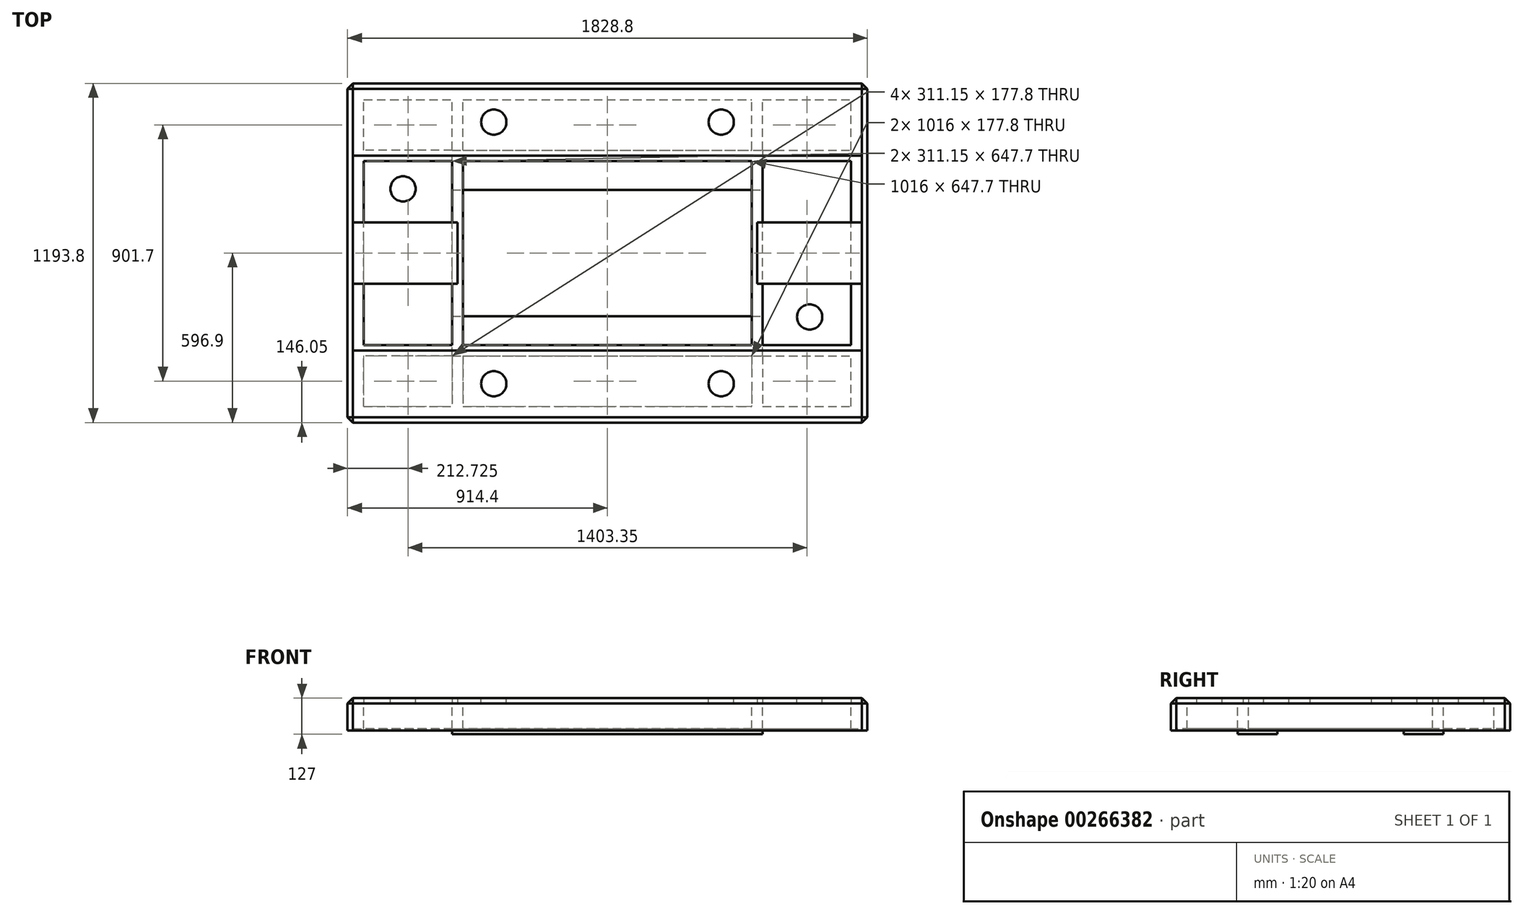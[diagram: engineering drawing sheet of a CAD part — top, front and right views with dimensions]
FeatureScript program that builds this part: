
annotation { "Feature Type Name" : "Feature", "Feature Type Description" : "" }
export const myFeature = defineFeature(function(context is Context, id is Id, definition is map)
    precondition{}
    {
        {
            var Q0;
            Q0=qCreatedBy(makeId("Top.planeOp"),FACE);
            var sketch = newSketch(context, id + "F0", { "sketchPlane" : qUnion([Q0])});
            skLineSegment(sketch, "E0.bottom", {"start": v(508, 323.85) * mm, "end": v(-508, 323.85) * mm});
            skLineSegment(sketch, "E0.top", {"start": v(508, -323.85) * mm, "end": v(-508, -323.85) * mm});
            skLineSegment(sketch, "E0.left", {"start": v(508, 323.85) * mm, "end": v(508, -323.85) * mm});
            skLineSegment(sketch, "E0.right", {"start": v(-508, 323.85) * mm, "end": v(-508, -323.85) * mm});
            skPoint(sketch, "E0.middle", {"position": v(0, 0) * mm});
            skLineSegment(sketch, "E1.bottom", {"start": v(-546.1, -361.95) * mm, "end": v(546.1, -361.95) * mm});
            skLineSegment(sketch, "E1.top", {"start": v(-546.1, 361.95) * mm, "end": v(546.1, 361.95) * mm});
            skLineSegment(sketch, "E1.left", {"start": v(-546.1, -361.95) * mm, "end": v(-546.1, 361.95) * mm});
            skLineSegment(sketch, "E1.right", {"start": v(546.1, -361.95) * mm, "end": v(546.1, 361.95) * mm});
            skLineSegment(sketch, "E2.bottom", {"start": v(-895.35, 577.85) * mm, "end": v(895.35, 577.85) * mm});
            skLineSegment(sketch, "E2.top", {"start": v(-895.35, -577.85) * mm, "end": v(895.35, -577.85) * mm});
            skLineSegment(sketch, "E2.left", {"start": v(-895.35, 577.85) * mm, "end": v(-895.35, -577.85) * mm});
            skLineSegment(sketch, "E2.right", {"start": v(895.35, 577.85) * mm, "end": v(895.35, -577.85) * mm});
            skLineSegment(sketch, "E3.bottom", {"start": v(-857.25, -539.75) * mm, "end": v(857.25, -539.75) * mm});
            skLineSegment(sketch, "E3.top", {"start": v(-857.25, 539.75) * mm, "end": v(857.25, 539.75) * mm});
            skLineSegment(sketch, "E3.left", {"start": v(-857.25, -539.75) * mm, "end": v(-857.25, 539.75) * mm});
            skLineSegment(sketch, "E3.right", {"start": v(857.25, -539.75) * mm, "end": v(857.25, 539.75) * mm});
            skLineSegment(sketch, "E4", {"start": v(-546.1, 361.95) * mm, "end": v(-895.35, 361.95) * mm});
            skLineSegment(sketch, "E5", {"start": v(-508, 323.85) * mm, "end": v(-895.35, 323.85) * mm});
            skLineSegment(sketch, "E6", {"start": v(-546.1, 361.95) * mm, "end": v(-546.1, 577.85) * mm});
            skLineSegment(sketch, "E7", {"start": v(-508, 323.85) * mm, "end": v(-508, 577.85) * mm});
            skLineSegment(sketch, "E8", {"start": v(546.1, 361.95) * mm, "end": v(546.1, 577.85) * mm});
            skLineSegment(sketch, "E9", {"start": v(508, 323.85) * mm, "end": v(508, 577.85) * mm});
            skLineSegment(sketch, "E10", {"start": v(508, -323.85) * mm, "end": v(508, -577.85) * mm});
            skLineSegment(sketch, "E11", {"start": v(546.1, -361.95) * mm, "end": v(546.1, -577.85) * mm});
            skLineSegment(sketch, "E12", {"start": v(546.1, -361.95) * mm, "end": v(895.35, -361.95) * mm});
            skLineSegment(sketch, "E13", {"start": v(508, -323.85) * mm, "end": v(895.35, -323.85) * mm});
            skLineSegment(sketch, "E14", {"start": v(-546.1, -361.95) * mm, "end": v(-895.35, -361.95) * mm});
            skLineSegment(sketch, "E15", {"start": v(-508, -323.85) * mm, "end": v(-895.35, -323.85) * mm});
            skLineSegment(sketch, "E16", {"start": v(546.1, 361.95) * mm, "end": v(895.35, 361.95) * mm});
            skLineSegment(sketch, "E17", {"start": v(508, 323.85) * mm, "end": v(895.35, 323.85) * mm});
            skLineSegment(sketch, "E18", {"start": v(-546.1, -361.95) * mm, "end": v(-546.1, -577.85) * mm});
            skLineSegment(sketch, "E19", {"start": v(-508, -323.85) * mm, "end": v(-508, -577.85) * mm});
            skSolve(sketch);
        }
        {
            var Q0;
            Q0 = qSketchRegion(id + "F0", true);
            var Q1;
            {var subQ3=sQuery(id+"F0.wireOp",EDGE,"E5");var subQ5=sQuery(id+"F0.wireOp",EDGE,"E3.left");var subQ6=makeQuery(id+"F0.imprint","INTERSECT",VERTEX,{"derivedFrom":[subQ5,subQ3]});Q1=makeQuery(id+"F0.imprint","IMPRINT",FACE,{"disambiguationData":[TD([[makeQuery(id+"F0.imprint","IMPRINT",EDGE,{"disambiguationData":[TD([[subQ6,-1.0]])],"derivedFrom":subQ5}),-1.0]])]});}
            var Q2;
            {var subQ0=sQuery(id+"F0.wireOp",EDGE,"E6");var subQ5=sQuery(id+"F0.wireOp",EDGE,"E3.top");var subQ7=makeQuery(id+"F0.imprint","INTERSECT",VERTEX,{"derivedFrom":[subQ5,subQ0]});Q2=makeQuery(id+"F0.imprint","IMPRINT",FACE,{"disambiguationData":[TD([[makeQuery(id+"F0.imprint","IMPRINT",EDGE,{"disambiguationData":[TD([[subQ7,-1.0]])],"derivedFrom":subQ5}),-1.0]])]});}
            var Q3;
            {var subQ1=sQuery(id+"F0.wireOp",EDGE,"E1.top");var subQ3=sQuery(id+"F0.wireOp",EDGE,"E7");var subQ4=makeQuery(id+"F0.imprint","INTERSECT",VERTEX,{"derivedFrom":[subQ1,subQ3]});Q3=makeQuery(id+"F0.imprint","IMPRINT",FACE,{"disambiguationData":[TD([[makeQuery(id+"F0.imprint","IMPRINT",EDGE,{"disambiguationData":[TD([[subQ4,1.0]])],"derivedFrom":subQ1}),-1.0]])]});}
            var Q4;
            {var subQ0=sQuery(id+"F0.wireOp",EDGE,"E0.right");Q4=makeQuery(id+"F0.imprint","IMPRINT",FACE,{"disambiguationData":[TD([[makeQuery(id+"F0.imprint","IMPRINT",EDGE,{"derivedFrom":subQ0}),-1.0]])]});}
            var Q5;
            {var subQ0=sQuery(id+"F0.wireOp",EDGE,"E14");var subQ5=sQuery(id+"F0.wireOp",EDGE,"E3.left");var subQ6=makeQuery(id+"F0.imprint","INTERSECT",VERTEX,{"derivedFrom":[subQ5,subQ0]});Q5=makeQuery(id+"F0.imprint","IMPRINT",FACE,{"disambiguationData":[TD([[makeQuery(id+"F0.imprint","IMPRINT",EDGE,{"disambiguationData":[TD([[subQ6,-1.0]])],"derivedFrom":subQ5}),-1.0]])]});}
            var Q6;
            {var subQ0=sQuery(id+"F0.wireOp",EDGE,"E18");var subQ5=sQuery(id+"F0.wireOp",EDGE,"E3.bottom");var subQ6=makeQuery(id+"F0.imprint","INTERSECT",VERTEX,{"derivedFrom":[subQ5,subQ0]});Q6=makeQuery(id+"F0.imprint","IMPRINT",FACE,{"disambiguationData":[TD([[makeQuery(id+"F0.imprint","IMPRINT",EDGE,{"disambiguationData":[TD([[subQ6,-1.0]])],"derivedFrom":subQ5}),1.0]])]});}
            var Q7;
            {var subQ1=sQuery(id+"F0.wireOp",EDGE,"E1.bottom");var subQ3=sQuery(id+"F0.wireOp",EDGE,"E19");var subQ4=makeQuery(id+"F0.imprint","INTERSECT",VERTEX,{"derivedFrom":[subQ1,subQ3]});Q7=makeQuery(id+"F0.imprint","IMPRINT",FACE,{"disambiguationData":[TD([[makeQuery(id+"F0.imprint","IMPRINT",EDGE,{"disambiguationData":[TD([[subQ4,1.0]])],"derivedFrom":subQ1}),1.0]])]});}
            var Q8;
            {var subQ0=sQuery(id+"F0.wireOp",EDGE,"E0.top");Q8=makeQuery(id+"F0.imprint","IMPRINT",FACE,{"disambiguationData":[TD([[makeQuery(id+"F0.imprint","IMPRINT",EDGE,{"derivedFrom":subQ0}),1.0]])]});}
            var Q9;
            {var subQ3=sQuery(id+"F0.wireOp",EDGE,"E10");var subQ5=sQuery(id+"F0.wireOp",EDGE,"E3.bottom");var subQ6=makeQuery(id+"F0.imprint","INTERSECT",VERTEX,{"derivedFrom":[subQ5,subQ3]});Q9=makeQuery(id+"F0.imprint","IMPRINT",FACE,{"disambiguationData":[TD([[makeQuery(id+"F0.imprint","IMPRINT",EDGE,{"disambiguationData":[TD([[subQ6,-1.0]])],"derivedFrom":subQ5}),1.0]])]});}
            var Q10;
            {var subQ1=sQuery(id+"F0.wireOp",EDGE,"E1.bottom");var subQ3=sQuery(id+"F0.wireOp",EDGE,"E10");var subQ4=makeQuery(id+"F0.imprint","INTERSECT",VERTEX,{"derivedFrom":[subQ1,subQ3]});Q10=makeQuery(id+"F0.imprint","IMPRINT",FACE,{"disambiguationData":[TD([[makeQuery(id+"F0.imprint","IMPRINT",EDGE,{"disambiguationData":[TD([[subQ4,-1.0]])],"derivedFrom":subQ1}),1.0]])]});}
            var Q11;
            {var subQ0=sQuery(id+"F0.wireOp",EDGE,"E12");var subQ5=sQuery(id+"F0.wireOp",EDGE,"E3.right");var subQ6=makeQuery(id+"F0.imprint","INTERSECT",VERTEX,{"derivedFrom":[subQ5,subQ0]});Q11=makeQuery(id+"F0.imprint","IMPRINT",FACE,{"disambiguationData":[TD([[makeQuery(id+"F0.imprint","IMPRINT",EDGE,{"disambiguationData":[TD([[subQ6,-1.0]])],"derivedFrom":subQ5}),1.0]])]});}
            var Q12;
            {var subQ0=sQuery(id+"F0.wireOp",EDGE,"E0.left");Q12=makeQuery(id+"F0.imprint","IMPRINT",FACE,{"disambiguationData":[TD([[makeQuery(id+"F0.imprint","IMPRINT",EDGE,{"derivedFrom":subQ0}),1.0]])]});}
            var Q13;
            {var subQ1=sQuery(id+"F0.wireOp",EDGE,"E1.top");var subQ3=sQuery(id+"F0.wireOp",EDGE,"E9");var subQ4=makeQuery(id+"F0.imprint","INTERSECT",VERTEX,{"derivedFrom":[subQ1,subQ3]});Q13=makeQuery(id+"F0.imprint","IMPRINT",FACE,{"disambiguationData":[TD([[makeQuery(id+"F0.imprint","IMPRINT",EDGE,{"disambiguationData":[TD([[subQ4,-1.0]])],"derivedFrom":subQ1}),-1.0]])]});}
            var Q14;
            {var subQ3=sQuery(id+"F0.wireOp",EDGE,"E9");var subQ5=sQuery(id+"F0.wireOp",EDGE,"E3.top");var subQ6=makeQuery(id+"F0.imprint","INTERSECT",VERTEX,{"derivedFrom":[subQ5,subQ3]});Q14=makeQuery(id+"F0.imprint","IMPRINT",FACE,{"disambiguationData":[TD([[makeQuery(id+"F0.imprint","IMPRINT",EDGE,{"disambiguationData":[TD([[subQ6,-1.0]])],"derivedFrom":subQ5}),-1.0]])]});}
            var Q15;
            {var subQ3=sQuery(id+"F0.wireOp",EDGE,"E17");var subQ5=sQuery(id+"F0.wireOp",EDGE,"E3.right");var subQ6=makeQuery(id+"F0.imprint","INTERSECT",VERTEX,{"derivedFrom":[subQ5,subQ3]});Q15=makeQuery(id+"F0.imprint","IMPRINT",FACE,{"disambiguationData":[TD([[makeQuery(id+"F0.imprint","IMPRINT",EDGE,{"disambiguationData":[TD([[subQ6,-1.0]])],"derivedFrom":subQ5}),1.0]])]});}
            var Q16;
            {var subQ0=sQuery(id+"F0.wireOp",EDGE,"E0.bottom");Q16=makeQuery(id+"F0.imprint","IMPRINT",FACE,{"disambiguationData":[TD([[makeQuery(id+"F0.imprint","IMPRINT",EDGE,{"derivedFrom":subQ0}),-1.0]])]});}
            extrude(context, id + "F1", {"entities" : qUnion([Q0, Q1, Q2, Q3, Q4, Q5, Q6, Q7, Q8, Q9, Q10, Q11, Q12, Q13, Q14, Q15, Q16]), "oppositeDirection" : true, "depth" : 88.9 * mm});
        }
        {
            var Q0;
            Q0=makeQuery(id+"F1.opExtrude","CAP_FACE",FACE,{"disambiguationData":[OSD([sQuery(id+"F0.wireOp",EDGE,"E0.bottom"),sQuery(id+"F0.wireOp",EDGE,"E0.top"),sQuery(id+"F0.wireOp",EDGE,"E0.left"),sQuery(id+"F0.wireOp",EDGE,"E0.right"),sQuery(id+"F0.wireOp",EDGE,"E1.bottom"),sQuery(id+"F0.wireOp",EDGE,"E1.top"),sQuery(id+"F0.wireOp",EDGE,"E1.left"),sQuery(id+"F0.wireOp",EDGE,"E1.right"),sQuery(id+"F0.wireOp",EDGE,"E2.bottom"),sQuery(id+"F0.wireOp",EDGE,"E2.top"),sQuery(id+"F0.wireOp",EDGE,"E2.left"),sQuery(id+"F0.wireOp",EDGE,"E2.right"),sQuery(id+"F0.wireOp",EDGE,"E3.bottom"),sQuery(id+"F0.wireOp",EDGE,"E3.top"),sQuery(id+"F0.wireOp",EDGE,"E3.left"),sQuery(id+"F0.wireOp",EDGE,"E3.right"),sQuery(id+"F0.wireOp",EDGE,"E4"),sQuery(id+"F0.wireOp",EDGE,"E5"),sQuery(id+"F0.wireOp",EDGE,"E6"),sQuery(id+"F0.wireOp",EDGE,"E7"),sQuery(id+"F0.wireOp",EDGE,"E8"),sQuery(id+"F0.wireOp",EDGE,"E9"),sQuery(id+"F0.wireOp",EDGE,"E10"),sQuery(id+"F0.wireOp",EDGE,"E11"),sQuery(id+"F0.wireOp",EDGE,"E12"),sQuery(id+"F0.wireOp",EDGE,"E13"),sQuery(id+"F0.wireOp",EDGE,"E14"),sQuery(id+"F0.wireOp",EDGE,"E15"),sQuery(id+"F0.wireOp",EDGE,"E16"),sQuery(id+"F0.wireOp",EDGE,"E17"),sQuery(id+"F0.wireOp",EDGE,"E18"),sQuery(id+"F0.wireOp",EDGE,"E19")])],"isStart":true});
            var sketch = newSketch(context, id + "F2", { "sketchPlane" : qUnion([Q0])});
            skLineSegment(sketch, "E20.bottom", {"start": v(-895.35, 577.85) * mm, "end": v(895.35, 577.85) * mm});
            skLineSegment(sketch, "E20.top", {"start": v(-895.35, 342.9) * mm, "end": v(895.35, 342.9) * mm});
            skLineSegment(sketch, "E20.left", {"start": v(-895.35, 577.85) * mm, "end": v(-895.35, 342.9) * mm});
            skLineSegment(sketch, "E20.right", {"start": v(895.35, 577.85) * mm, "end": v(895.35, 342.9) * mm});
            skLineSegment(sketch, "E21.bottom", {"start": v(-895.35, -577.85) * mm, "end": v(895.35, -577.85) * mm});
            skLineSegment(sketch, "E21.top", {"start": v(-895.35, -342.9) * mm, "end": v(895.35, -342.9) * mm});
            skLineSegment(sketch, "E21.left", {"start": v(-895.35, -577.85) * mm, "end": v(-895.35, -342.9) * mm});
            skLineSegment(sketch, "E21.right", {"start": v(895.35, -577.85) * mm, "end": v(895.35, -342.9) * mm});
            skLineSegment(sketch, "E22.bottom", {"start": v(-895.35, -342.9) * mm, "end": v(-527.05, -342.9) * mm});
            skLineSegment(sketch, "E22.top", {"start": v(-895.35, -107.95) * mm, "end": v(-527.05, -107.95) * mm});
            skLineSegment(sketch, "E22.left", {"start": v(-895.35, -342.9) * mm, "end": v(-895.35, -107.95) * mm});
            skLineSegment(sketch, "E22.right", {"start": v(-527.05, -342.9) * mm, "end": v(-527.05, -107.95) * mm});
            skLineSegment(sketch, "E23.bottom", {"start": v(-895.35, 342.9) * mm, "end": v(-527.05, 342.9) * mm});
            skLineSegment(sketch, "E23.top", {"start": v(-895.35, 107.95) * mm, "end": v(-527.05, 107.95) * mm});
            skLineSegment(sketch, "E23.left", {"start": v(-895.35, 342.9) * mm, "end": v(-895.35, 107.95) * mm});
            skLineSegment(sketch, "E23.right", {"start": v(-527.05, 342.9) * mm, "end": v(-527.05, 107.95) * mm});
            skLineSegment(sketch, "E24.left", {"start": v(-895.35, 107.95) * mm, "end": v(-895.35, -107.95) * mm});
            skLineSegment(sketch, "E24.right", {"start": v(-527.05, 107.95) * mm, "end": v(-527.05, -107.95) * mm});
            skLineSegment(sketch, "E25.bottom", {"start": v(895.35, 342.9) * mm, "end": v(527.05, 342.9) * mm});
            skLineSegment(sketch, "E25.top", {"start": v(895.35, 107.95) * mm, "end": v(527.05, 107.95) * mm});
            skLineSegment(sketch, "E25.left", {"start": v(895.35, 342.9) * mm, "end": v(895.35, 107.95) * mm});
            skLineSegment(sketch, "E25.right", {"start": v(527.05, 342.9) * mm, "end": v(527.05, 107.95) * mm});
            skLineSegment(sketch, "E26.bottom", {"start": v(895.35, -342.9) * mm, "end": v(527.05, -342.9) * mm});
            skLineSegment(sketch, "E26.top", {"start": v(895.35, -107.95) * mm, "end": v(527.05, -107.95) * mm});
            skLineSegment(sketch, "E26.left", {"start": v(895.35, -342.9) * mm, "end": v(895.35, -107.95) * mm});
            skLineSegment(sketch, "E26.right", {"start": v(527.05, -342.9) * mm, "end": v(527.05, -107.95) * mm});
            skLineSegment(sketch, "E27.left", {"start": v(895.35, 107.95) * mm, "end": v(895.35, -107.95) * mm});
            skLineSegment(sketch, "E27.right", {"start": v(527.05, 107.95) * mm, "end": v(527.05, -107.95) * mm});
            skSolve(sketch);
        }
        {
            var Q0;
            Q0=makeQuery(id+"F2.imprint","IMPRINT",FACE,{"disambiguationData":[TD([[makeQuery(id+"F2.imprint","IMPRINT",EDGE,{"derivedFrom":sQuery(id+"F2.wireOp",EDGE,"E20.bottom")}),-1.0]])]});
            var Q1;
            {var subQ4=sQuery(id+"F0.wireOp",EDGE,"E4");Q1=makeQuery(id+"F2.imprint","IMPRINT",FACE,{"disambiguationData":[TD([[makeQuery(id+"F2.imprint","IMPRINT",EDGE,{"derivedFrom":makeQuery(id+"F1.opExtrude","CAP_EDGE",EDGE,{"disambiguationData":[OSD([subQ4])],"isStart":true})}),-1.0]])]});}
            var Q2;
            Q2=makeQuery(id+"F2.imprint","IMPRINT",FACE,{"disambiguationData":[TD([[makeQuery(id+"F2.imprint","IMPRINT",EDGE,{"derivedFrom":makeQuery(id+"F1.opExtrude","CAP_EDGE",EDGE,{"disambiguationData":[OSD([sQuery(id+"F0.wireOp",EDGE,"E1.top")])],"isStart":true})}),1.0]])]});
            var Q3;
            {var subQ0=sQuery(id+"F2.wireOp",EDGE,"E25.top");var subQ4=makeQuery(id+"F1.opExtrude","CAP_EDGE",EDGE,{"disambiguationData":[OSD([sQuery(id+"F0.wireOp",EDGE,"E1.right")])],"isStart":true});var subQ5=makeQuery(id+"F2.imprint","INTERSECT",VERTEX,{"derivedFrom":[subQ4,subQ0]});Q3=makeQuery(id+"F2.imprint","IMPRINT",FACE,{"disambiguationData":[TD([[makeQuery(id+"F2.imprint","IMPRINT",EDGE,{"disambiguationData":[TD([[subQ5,1.0]])],"derivedFrom":subQ4}),-1.0]])]});}
            var Q4;
            {var subQ0=sQuery(id+"F2.wireOp",EDGE,"E27.left");Q4=makeQuery(id+"F2.imprint","IMPRINT",FACE,{"disambiguationData":[TD([[makeQuery(id+"F2.imprint","IMPRINT",EDGE,{"derivedFrom":subQ0}),-1.0]])]});}
            var Q5;
            {var subQ0=sQuery(id+"F2.wireOp",EDGE,"E27.right");Q5=makeQuery(id+"F2.imprint","IMPRINT",FACE,{"disambiguationData":[TD([[makeQuery(id+"F2.imprint","IMPRINT",EDGE,{"derivedFrom":subQ0}),1.0]])]});}
            var Q6;
            {var subQ0=sQuery(id+"F2.wireOp",EDGE,"E23.top");var subQ4=makeQuery(id+"F1.opExtrude","CAP_EDGE",EDGE,{"disambiguationData":[OSD([sQuery(id+"F0.wireOp",EDGE,"E1.left")])],"isStart":true});var subQ5=makeQuery(id+"F2.imprint","INTERSECT",VERTEX,{"derivedFrom":[subQ4,subQ0]});Q6=makeQuery(id+"F2.imprint","IMPRINT",FACE,{"disambiguationData":[TD([[makeQuery(id+"F2.imprint","IMPRINT",EDGE,{"disambiguationData":[TD([[subQ5,1.0]])],"derivedFrom":subQ4}),1.0]])]});}
            var Q7;
            {var subQ0=sQuery(id+"F2.wireOp",EDGE,"E24.left");Q7=makeQuery(id+"F2.imprint","IMPRINT",FACE,{"disambiguationData":[TD([[makeQuery(id+"F2.imprint","IMPRINT",EDGE,{"derivedFrom":subQ0}),1.0]])]});}
            var Q8;
            {var subQ0=sQuery(id+"F2.wireOp",EDGE,"E24.right");Q8=makeQuery(id+"F2.imprint","IMPRINT",FACE,{"disambiguationData":[TD([[makeQuery(id+"F2.imprint","IMPRINT",EDGE,{"derivedFrom":subQ0}),-1.0]])]});}
            var Q9;
            Q9=makeQuery(id+"F2.imprint","IMPRINT",FACE,{"disambiguationData":[TD([[makeQuery(id+"F2.imprint","IMPRINT",EDGE,{"derivedFrom":sQuery(id+"F2.wireOp",EDGE,"E21.bottom")}),1.0]])]});
            var Q10;
            {var subQ4=sQuery(id+"F0.wireOp",EDGE,"E14");Q10=makeQuery(id+"F2.imprint","IMPRINT",FACE,{"disambiguationData":[TD([[makeQuery(id+"F2.imprint","IMPRINT",EDGE,{"derivedFrom":makeQuery(id+"F1.opExtrude","CAP_EDGE",EDGE,{"disambiguationData":[OSD([subQ4])],"isStart":true})}),1.0]])]});}
            var Q11;
            Q11=makeQuery(id+"F2.imprint","IMPRINT",FACE,{"disambiguationData":[TD([[makeQuery(id+"F2.imprint","IMPRINT",EDGE,{"derivedFrom":makeQuery(id+"F1.opExtrude","CAP_EDGE",EDGE,{"disambiguationData":[OSD([sQuery(id+"F0.wireOp",EDGE,"E1.bottom")])],"isStart":true})}),-1.0]])]});
            var Q12;
            {var subQ3=sQuery(id+"F0.wireOp",EDGE,"E11");Q12=makeQuery(id+"F2.imprint","IMPRINT",FACE,{"disambiguationData":[TD([[makeQuery(id+"F2.imprint","IMPRINT",EDGE,{"derivedFrom":makeQuery(id+"F1.opExtrude","CAP_EDGE",EDGE,{"disambiguationData":[OSD([subQ3])],"isStart":true})}),1.0]])]});}
            var Q13;
            {var subQ3=sQuery(id+"F0.wireOp",EDGE,"E8");Q13=makeQuery(id+"F2.imprint","IMPRINT",FACE,{"disambiguationData":[TD([[makeQuery(id+"F2.imprint","IMPRINT",EDGE,{"derivedFrom":makeQuery(id+"F1.opExtrude","CAP_EDGE",EDGE,{"disambiguationData":[OSD([subQ3])],"isStart":true})}),-1.0]])]});}
            extrude(context, id + "F3", {"entities" : qUnion([Q0, Q1, Q2, Q3, Q4, Q5, Q6, Q7, Q8, Q9, Q10, Q11, Q12, Q13]), "depth" : 19.05 * mm});
        }
        {
            var Q0;
            {var subQ2=sQuery(id+"F0.wireOp",EDGE,"E5");var subQ7=makeQuery(id+"F1.opExtrude","CAP_EDGE",EDGE,{"disambiguationData":[OSD([subQ2])],"isStart":true});Q0=makeQuery(id+"F2.imprint","IMPRINT",FACE,{"disambiguationData":[TD([[makeQuery(id+"F2.imprint","IMPRINT",EDGE,{"derivedFrom":subQ7}),1.0]])]});}
            var Q1;
            Q1=makeQuery(id+"F2.imprint","IMPRINT",FACE,{"disambiguationData":[TD([[makeQuery(id+"F2.imprint","IMPRINT",EDGE,{"derivedFrom":sQuery(id+"F2.wireOp",EDGE,"E23.bottom")}),-1.0]])]});
            var Q2;
            Q2=makeQuery(id+"F2.imprint","IMPRINT",FACE,{"disambiguationData":[TD([[makeQuery(id+"F2.imprint","IMPRINT",EDGE,{"derivedFrom":sQuery(id+"F2.wireOp",EDGE,"E25.bottom")}),1.0]])]});
            var Q3;
            {var subQ2=sQuery(id+"F0.wireOp",EDGE,"E17");var subQ7=makeQuery(id+"F1.opExtrude","CAP_EDGE",EDGE,{"disambiguationData":[OSD([subQ2])],"isStart":true});Q3=makeQuery(id+"F2.imprint","IMPRINT",FACE,{"disambiguationData":[TD([[makeQuery(id+"F2.imprint","IMPRINT",EDGE,{"derivedFrom":subQ7}),-1.0]])]});}
            var Q4;
            Q4=makeQuery(id+"F2.imprint","IMPRINT",FACE,{"disambiguationData":[TD([[makeQuery(id+"F2.imprint","IMPRINT",EDGE,{"derivedFrom":sQuery(id+"F2.wireOp",EDGE,"E26.bottom")}),-1.0]])]});
            var Q5;
            {var subQ1=sQuery(id+"F0.wireOp",EDGE,"E13");var subQ7=makeQuery(id+"F1.opExtrude","CAP_EDGE",EDGE,{"disambiguationData":[OSD([subQ1])],"isStart":true});Q5=makeQuery(id+"F2.imprint","IMPRINT",FACE,{"disambiguationData":[TD([[makeQuery(id+"F2.imprint","IMPRINT",EDGE,{"derivedFrom":subQ7}),1.0]])]});}
            var Q6;
            Q6=makeQuery(id+"F2.imprint","IMPRINT",FACE,{"disambiguationData":[TD([[makeQuery(id+"F2.imprint","IMPRINT",EDGE,{"derivedFrom":sQuery(id+"F2.wireOp",EDGE,"E22.bottom")}),1.0]])]});
            var Q7;
            {var subQ1=sQuery(id+"F0.wireOp",EDGE,"E15");var subQ7=makeQuery(id+"F1.opExtrude","CAP_EDGE",EDGE,{"disambiguationData":[OSD([subQ1])],"isStart":true});Q7=makeQuery(id+"F2.imprint","IMPRINT",FACE,{"disambiguationData":[TD([[makeQuery(id+"F2.imprint","IMPRINT",EDGE,{"derivedFrom":subQ7}),-1.0]])]});}
            extrude(context, id + "F4", {"entities" : qUnion([Q0, Q1, Q2, Q3, Q4, Q5, Q6, Q7]), "depth" : 19.05 * mm});
        }
        {
            var Q0;
            Q0=makeQuery(id+"F1.opExtrude","CAP_FACE",FACE,{"disambiguationData":[OSD([sQuery(id+"F0.wireOp",EDGE,"E0.bottom"),sQuery(id+"F0.wireOp",EDGE,"E0.top"),sQuery(id+"F0.wireOp",EDGE,"E0.left"),sQuery(id+"F0.wireOp",EDGE,"E0.right"),sQuery(id+"F0.wireOp",EDGE,"E1.bottom"),sQuery(id+"F0.wireOp",EDGE,"E1.top"),sQuery(id+"F0.wireOp",EDGE,"E1.left"),sQuery(id+"F0.wireOp",EDGE,"E1.right"),sQuery(id+"F0.wireOp",EDGE,"E2.bottom"),sQuery(id+"F0.wireOp",EDGE,"E2.top"),sQuery(id+"F0.wireOp",EDGE,"E2.left"),sQuery(id+"F0.wireOp",EDGE,"E2.right"),sQuery(id+"F0.wireOp",EDGE,"E3.bottom"),sQuery(id+"F0.wireOp",EDGE,"E3.top"),sQuery(id+"F0.wireOp",EDGE,"E3.left"),sQuery(id+"F0.wireOp",EDGE,"E3.right"),sQuery(id+"F0.wireOp",EDGE,"E4"),sQuery(id+"F0.wireOp",EDGE,"E5"),sQuery(id+"F0.wireOp",EDGE,"E6"),sQuery(id+"F0.wireOp",EDGE,"E7"),sQuery(id+"F0.wireOp",EDGE,"E8"),sQuery(id+"F0.wireOp",EDGE,"E9"),sQuery(id+"F0.wireOp",EDGE,"E10"),sQuery(id+"F0.wireOp",EDGE,"E11"),sQuery(id+"F0.wireOp",EDGE,"E12"),sQuery(id+"F0.wireOp",EDGE,"E13"),sQuery(id+"F0.wireOp",EDGE,"E14"),sQuery(id+"F0.wireOp",EDGE,"E15"),sQuery(id+"F0.wireOp",EDGE,"E16"),sQuery(id+"F0.wireOp",EDGE,"E17"),sQuery(id+"F0.wireOp",EDGE,"E18"),sQuery(id+"F0.wireOp",EDGE,"E19")])],"isStart":false});
            var sketch = newSketch(context, id + "F5", { "sketchPlane" : qUnion([Q0])});
            skLineSegment(sketch, "E28.bottom", {"start": v(-546.1, 361.95) * mm, "end": v(546.1, 361.95) * mm});
            skLineSegment(sketch, "E28.top", {"start": v(-546.1, 222.25) * mm, "end": v(546.1, 222.25) * mm});
            skLineSegment(sketch, "E28.left", {"start": v(-546.1, 361.95) * mm, "end": v(-546.1, 222.25) * mm});
            skLineSegment(sketch, "E28.right", {"start": v(546.1, 361.95) * mm, "end": v(546.1, 222.25) * mm});
            skLineSegment(sketch, "E29.bottom", {"start": v(-546.1, -361.95) * mm, "end": v(546.1, -361.95) * mm});
            skLineSegment(sketch, "E29.top", {"start": v(-546.1, -222.25) * mm, "end": v(546.1, -222.25) * mm});
            skLineSegment(sketch, "E29.left", {"start": v(-546.1, -361.95) * mm, "end": v(-546.1, -222.25) * mm});
            skLineSegment(sketch, "E29.right", {"start": v(546.1, -361.95) * mm, "end": v(546.1, -222.25) * mm});
            skSolve(sketch);
        }
        {
            var Q0;
            Q0 = qSketchRegion(id + "F5", true);
            extrude(context, id + "F6", {"entities" : qUnion([Q0]), "depth" : 19.05 * mm});
        }
        {
            var Q0;
            Q0=makeQuery(id+"F3.opExtrude","SWEPT_FACE",FACE,{"disambiguationData":[OSD([sQuery(id+"F2.wireOp",EDGE,"E21.bottom")])]});
            var sketch = newSketch(context, id + "F7", { "sketchPlane" : qUnion([Q0])});
            skLineSegment(sketch, "E30.bottom", {"start": v(-895.35, 19.05) * mm, "end": v(895.35, 19.05) * mm});
            skLineSegment(sketch, "E30.top", {"start": v(-895.35, -95.25) * mm, "end": v(895.35, -95.25) * mm});
            skLineSegment(sketch, "E30.left", {"start": v(-895.35, 19.05) * mm, "end": v(-895.35, -95.25) * mm});
            skLineSegment(sketch, "E30.right", {"start": v(895.35, 19.05) * mm, "end": v(895.35, -95.25) * mm});
            skSolve(sketch);
        }
        {
            var Q0;
            Q0 = qSketchRegion(id + "F7", true);
            extrude(context, id + "F8", {"entities" : qUnion([Q0]), "depth" : 19.05 * mm});
        }
        {
            var Q0;
            Q0=makeQuery(id+"F3.opExtrude","SWEPT_FACE",FACE,{"disambiguationData":[OSD([sQuery(id+"F2.wireOp",EDGE,"E20.bottom")])]});
            var sketch = newSketch(context, id + "F9", { "sketchPlane" : qUnion([Q0])});
            skLineSegment(sketch, "E31.bottom", {"start": v(-895.35, 19.05) * mm, "end": v(895.35, 19.05) * mm});
            skLineSegment(sketch, "E31.top", {"start": v(-895.35, -95.25) * mm, "end": v(895.35, -95.25) * mm});
            skLineSegment(sketch, "E31.left", {"start": v(-895.35, 19.05) * mm, "end": v(-895.35, -95.25) * mm});
            skLineSegment(sketch, "E31.right", {"start": v(895.35, 19.05) * mm, "end": v(895.35, -95.25) * mm});
            skSolve(sketch);
        }
        {
            var Q0;
            Q0 = qSketchRegion(id + "F9", true);
            extrude(context, id + "F10", {"entities" : qUnion([Q0]), "depth" : 19.05 * mm});
        }
        {
            var Q0;
            Q0=makeQuery(id+"F8.opExtrude","SWEPT_FACE",FACE,{"disambiguationData":[OSD([sQuery(id+"F7.wireOp",EDGE,"E30.right")])]});
            var sketch = newSketch(context, id + "F11", { "sketchPlane" : qUnion([Q0])});
            skLineSegment(sketch, "E32.bottom", {"start": v(-596.9, 19.05) * mm, "end": v(596.9, 19.05) * mm});
            skLineSegment(sketch, "E32.top", {"start": v(-596.9, -95.25) * mm, "end": v(596.9, -95.25) * mm});
            skLineSegment(sketch, "E32.left", {"start": v(-596.9, 19.05) * mm, "end": v(-596.9, -95.25) * mm});
            skLineSegment(sketch, "E32.right", {"start": v(596.9, 19.05) * mm, "end": v(596.9, -95.25) * mm});
            skSolve(sketch);
        }
        {
            var Q0;
            Q0 = qSketchRegion(id + "F11", true);
            extrude(context, id + "F12", {"entities" : qUnion([Q0]), "depth" : 19.05 * mm});
        }
        {
            var Q0;
            Q0=makeQuery(id+"F10.opExtrude","SWEPT_FACE",FACE,{"disambiguationData":[OSD([sQuery(id+"F9.wireOp",EDGE,"E31.right")])]});
            var sketch = newSketch(context, id + "F13", { "sketchPlane" : qUnion([Q0])});
            skLineSegment(sketch, "E33.bottom", {"start": v(-596.9, 19.05) * mm, "end": v(596.9, 19.05) * mm});
            skLineSegment(sketch, "E33.top", {"start": v(-596.9, -95.25) * mm, "end": v(596.9, -95.25) * mm});
            skLineSegment(sketch, "E33.left", {"start": v(-596.9, 19.05) * mm, "end": v(-596.9, -95.25) * mm});
            skLineSegment(sketch, "E33.right", {"start": v(596.9, 19.05) * mm, "end": v(596.9, -95.25) * mm});
            skSolve(sketch);
        }
        {
            var Q0;
            Q0 = qSketchRegion(id + "F13", true);
            extrude(context, id + "F14", {"entities" : qUnion([Q0]), "depth" : 19.05 * mm});
        }
        {
            var Q0;
            Q0=makeQuery(id+"F14.opExtrude","CAP_EDGE",EDGE,{"disambiguationData":[OSD([sQuery(id+"F13.wireOp",EDGE,"E33.bottom")])],"isStart":false});
            var Q1;
            Q1=makeQuery(id+"F10.opExtrude","CAP_EDGE",EDGE,{"disambiguationData":[OSD([sQuery(id+"F9.wireOp",EDGE,"E31.bottom")])],"isStart":false});
            var Q2;
            Q2=makeQuery(id+"F14.opExtrude","CAP_EDGE",EDGE,{"disambiguationData":[OSD([sQuery(id+"F13.wireOp",EDGE,"E33.left")])],"isStart":false});
            var Q3;
            Q3=makeQuery(id+"F14.opExtrude","CAP_EDGE",EDGE,{"disambiguationData":[OSD([sQuery(id+"F13.wireOp",EDGE,"E33.right")])],"isStart":false});
            var Q4;
            Q4=makeQuery(id+"F8.opExtrude","CAP_EDGE",EDGE,{"disambiguationData":[OSD([sQuery(id+"F7.wireOp",EDGE,"E30.bottom")])],"isStart":false});
            var Q5;
            Q5=makeQuery(id+"F12.opExtrude","CAP_EDGE",EDGE,{"disambiguationData":[OSD([sQuery(id+"F11.wireOp",EDGE,"E32.bottom")])],"isStart":false});
            var Q6;
            Q6=makeQuery(id+"F12.opExtrude","CAP_EDGE",EDGE,{"disambiguationData":[OSD([sQuery(id+"F11.wireOp",EDGE,"E32.left")])],"isStart":false});
            var Q7;
            Q7=makeQuery(id+"F12.opExtrude","CAP_EDGE",EDGE,{"disambiguationData":[OSD([sQuery(id+"F11.wireOp",EDGE,"E32.right")])],"isStart":false});
            var Q8;
            Q8=makeQuery(id+"F12.opExtrude","SWEPT_EDGE",EDGE,{"disambiguationData":[OSD([sQuery(id+"F11.wireOp",EDGE,"E32.bottom"),sQuery(id+"F11.wireOp",EDGE,"E32.right")])]});
            var Q9;
            Q9=makeQuery(id+"F12.opExtrude","SWEPT_EDGE",EDGE,{"disambiguationData":[OSD([sQuery(id+"F11.wireOp",EDGE,"E32.bottom"),sQuery(id+"F11.wireOp",EDGE,"E32.left")])]});
            var Q10;
            Q10=makeQuery(id+"F14.opExtrude","SWEPT_EDGE",EDGE,{"disambiguationData":[OSD([sQuery(id+"F13.wireOp",EDGE,"E33.bottom"),sQuery(id+"F13.wireOp",EDGE,"E33.right")])]});
            var Q11;
            Q11=makeQuery(id+"F14.opExtrude","SWEPT_EDGE",EDGE,{"disambiguationData":[OSD([sQuery(id+"F13.wireOp",EDGE,"E33.bottom"),sQuery(id+"F13.wireOp",EDGE,"E33.left")])]});
            chamfer(context, id + "F15", {"entities" : qUnion([Q0, Q1, Q2, Q3, Q4, Q5, Q6, Q7, Q8, Q9, Q10, Q11]), "width" : 19.05 * mm, "tangentPropagation" : true});
        }
        {
            var Q0;
            Q0=makeQuery(id+"F4.opExtrude","CAP_FACE",FACE,{"disambiguationData":[OSD([sQuery(id+"F2.wireOp",EDGE,"E23.bottom"),sQuery(id+"F2.wireOp",EDGE,"E23.left"),sQuery(id+"F2.wireOp",EDGE,"E23.right"),sQuery(id+"F2.wireOp",EDGE,"E23.top")])],"isStart":false});
            var sketch = newSketch(context, id + "F16", { "sketchPlane" : qUnion([Q0])});
            skLineSegment(sketch, "E34", {"start": v(-895.35, 225.43) * mm, "end": v(-527.05, 225.43) * mm});
            skLineSegment(sketch, "E35", {"start": v(-719.38, 342.9) * mm, "end": v(-719.38, 107.95) * mm});
            skCircle(sketch, "E36", {"center": v(-719.38, 225.43) * mm, "radius": 44.45 * mm});
            skLineSegment(sketch, "E37", {"start": v(-527.05, 225.43) * mm, "end": v(527.05, 225.43) * mm});
            skLineSegment(sketch, "E38", {"start": v(527.05, 225.43) * mm, "end": v(527.05, 0) * mm});
            skLineSegment(sketch, "E39", {"start": v(527.05, 0) * mm, "end": v(527.05, -225.43) * mm});
            skLineSegment(sketch, "E40", {"start": v(527.05, -225.43) * mm, "end": v(895.35, -225.43) * mm});
            skCircle(sketch, "E41", {"center": v(711.2, -225.43) * mm, "radius": 44.45 * mm});
            skLineSegment(sketch, "E42", {"start": v(-527.05, 225.43) * mm, "end": v(-527.05, 342.9) * mm});
            skLineSegment(sketch, "E43", {"start": v(-527.05, 342.9) * mm, "end": v(-527.05, 460.38) * mm});
            skLineSegment(sketch, "E44", {"start": v(527.05, 225.43) * mm, "end": v(527.05, 460.38) * mm});
            skLineSegment(sketch, "E45", {"start": v(527.05, 460.38) * mm, "end": v(895.35, 460.38) * mm});
            skLineSegment(sketch, "E46", {"start": v(-527.05, 460.38) * mm, "end": v(-895.35, 460.38) * mm});
            skLineSegment(sketch, "E47", {"start": v(-527.05, 460.38) * mm, "end": v(-400.05, 460.38) * mm});
            skLineSegment(sketch, "E48", {"start": v(527.05, 460.38) * mm, "end": v(400.05, 460.38) * mm});
            skLineSegment(sketch, "E49", {"start": v(527.05, -225.43) * mm, "end": v(527.05, -460.38) * mm});
            skLineSegment(sketch, "E50", {"start": v(527.05, -342.9) * mm, "end": v(-527.05, -342.9) * mm});
            skLineSegment(sketch, "E51", {"start": v(-527.05, -342.9) * mm, "end": v(-527.05, -460.38) * mm});
            skLineSegment(sketch, "E52", {"start": v(-527.05, -460.38) * mm, "end": v(-400.05, -460.38) * mm});
            skLineSegment(sketch, "E53", {"start": v(527.05, -460.38) * mm, "end": v(400.05, -460.38) * mm});
            skCircle(sketch, "E54", {"center": v(-400.05, 460.38) * mm, "radius": 44.45 * mm});
            skCircle(sketch, "E55", {"center": v(400.05, 460.38) * mm, "radius": 44.45 * mm});
            skCircle(sketch, "E56", {"center": v(400.05, -460.38) * mm, "radius": 44.45 * mm});
            skCircle(sketch, "E57", {"center": v(-400.05, -460.38) * mm, "radius": 44.45 * mm});
            skSolve(sketch);
        }
        {
            var Q0;
            Q0 = qSketchRegion(id + "F16", true);
            extrude(context, id + "F17", {"entities" : qUnion([Q0]), "operationType" : NewBodyOperationType.REMOVE, "oppositeDirection" : true, "depth" : 19.05 * mm});
        }
    });
